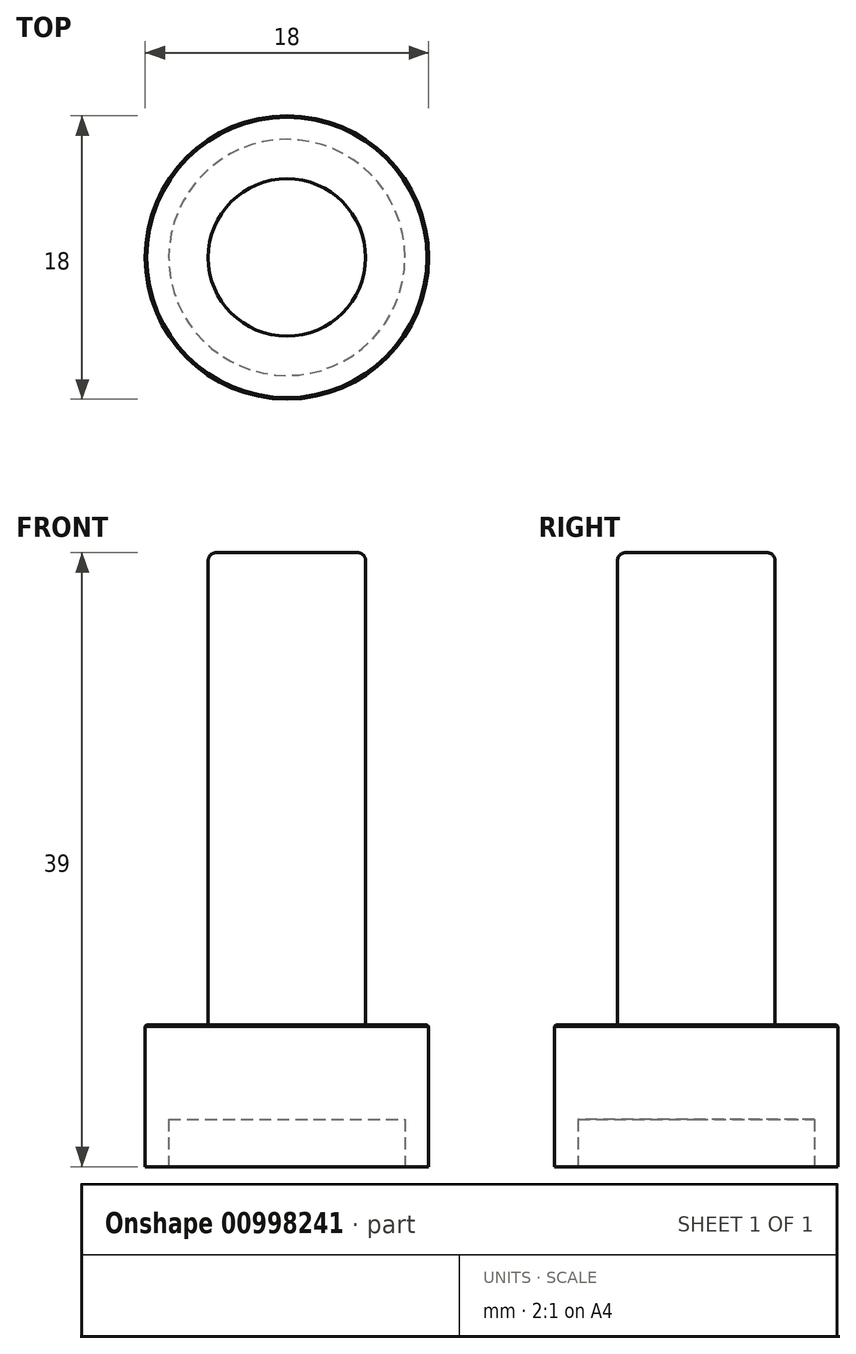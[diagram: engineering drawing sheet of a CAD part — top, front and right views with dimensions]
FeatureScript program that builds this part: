
annotation { "Feature Type Name" : "Feature", "Feature Type Description" : "" }
export const myFeature = defineFeature(function(context is Context, id is Id, definition is map)
    precondition{}
    {
        {
            var Q0;
            Q0=qCreatedBy(makeId("Top.planeOp"),FACE);
            var sketch = newSketch(context, id + "F0", { "sketchPlane" : qUnion([Q0])});
            skCircle(sketch, "E0", {"center": v(0, 0) * mm, "radius": 9 * mm});
            skSolve(sketch);
        }
        {
            var Q0;
            Q0 = qSketchRegion(id + "F0", true);
            extrude(context, id + "F1", {"entities" : qUnion([Q0]), "depth" : 9 * mm, "offsetDistance" : 25 * mm});
        }
        {
            var Q0;
            Q0=makeQuery(id+"F1.opExtrude","CAP_FACE",FACE,{"disambiguationData":[OSD([sQuery(id+"F0.wireOp",EDGE,"E0")])],"isStart":false});
            var sketch = newSketch(context, id + "F2", { "sketchPlane" : qUnion([Q0])});
            skCircle(sketch, "E1", {"center": v(0, 0) * mm, "radius": 5 * mm});
            skSolve(sketch);
        }
        {
            var Q0;
            Q0=makeQuery(id+"F2.imprint","IMPRINT",FACE,{"disambiguationData":[TD([[makeQuery(id+"F2.imprint","IMPRINT",EDGE,{"derivedFrom":sQuery(id+"F2.wireOp",EDGE,"E1")}),1.0]])]});
            extrude(context, id + "F3", {"entities" : qUnion([Q0]), "operationType" : NewBodyOperationType.ADD, "depth" : 30 * mm, "offsetDistance" : 25 * mm});
        }
        {
            var Q0;
            Q0=makeQuery(id+"F1.opExtrude","CAP_FACE",FACE,{"disambiguationData":[OSD([sQuery(id+"F0.wireOp",EDGE,"E0")])],"isStart":true});
            var sketch = newSketch(context, id + "F4", { "sketchPlane" : qUnion([Q0])});
            skCircle(sketch, "E2", {"center": v(0, 0) * mm, "radius": 7.5 * mm});
            skSolve(sketch);
        }
        {
            var Q0;
            Q0=makeQuery(id+"F4.imprint","IMPRINT",FACE,{"disambiguationData":[TD([[makeQuery(id+"F4.imprint","IMPRINT",EDGE,{"derivedFrom":sQuery(id+"F4.wireOp",EDGE,"E2")}),1.0]])]});
            extrude(context, id + "F5", {"entities" : qUnion([Q0]), "operationType" : NewBodyOperationType.REMOVE, "oppositeDirection" : true, "depth" : 3 * mm, "offsetDistance" : 25 * mm});
        }
        {
            var Q0;
            Q0=makeQuery(id+"F5.boolean.opBoolean","COPY",EDGE,{"derivedFrom":makeQuery(id+"F5.opExtrude","CAP_EDGE",EDGE,{"disambiguationData":[OSD([sQuery(id+"F4.wireOp",EDGE,"E2")])],"isStart":true})});
            var Q1;
            Q1=makeQuery(id+"F3.opExtrude","CAP_EDGE",EDGE,{"disambiguationData":[OSD([sQuery(id+"F2.wireOp",EDGE,"E1")])],"isStart":false});
            fillet(context, id + "F6", {"entities" : qUnion([Q0, Q1]), "radius" : .5 * mm, "tangentPropagation" : true, "allowEdgeOverflow" : false});
        }
        {
            var Q0;
            Q0=makeQuery(id+"F1.opExtrude","CAP_EDGE",EDGE,{"disambiguationData":[OSD([sQuery(id+"F0.wireOp",EDGE,"E0")])],"isStart":false});
            chamfer(context, id + "F7", {"entities" : qUnion([Q0]), "width" : .1 * mm, "tangentPropagation" : true});
        }
    });
